# Revit family: Washer_Milnor_35lb-45lb-Capacity_MWT16-18
name_source: partatom
category: Mechanical Equipment
units: mm (PartAtom-declared; Revit-internal decimal feet)

## family parameters
Always vertical = No
Cut with Voids When Loaded = No
Maintain Annotation Orientation = No
OmniClass Number = 23.45.70.11.14.11
OmniClass Title = Washing Machines
Part Type = Normal
Room Calculation Point = No
Round Connector Dimension = Use Diameter
Shared = No
Work Plane-Based = Yes

## types (2) — shared parameters
Assembly Code = E1010610
Construction Details = https://www.arcat.com
Cylinder Depth = 1' - 10"
Cylinder Diameter = 2' - 6"
Default Elevation = 4' - 0"
Description = Milnor Commercial Washer Extractor
Door Base from FF = 1' - 8 1/4"
Door Opening = 1' - 6"
Door Opening Depth = 1' - 5 5/8"
Dynamic Load = 0.00 kip
Expected Lifespan (Years) = 12
Extraction G-Force = 90 Gs
Frequency = 60 Hz
Green Building-LEED = https://www.arcat.com
Installation-Fabrication = https://www.arcat.com
Keynote = 11110
MEP Amperage = 7 A
Manufacturer = Pellerin Milnor Corp
Manufacturer Fax = 504-468-3094
Manufacturer Website = http://www.milnor.com
Number of Poles = 1
Overall Depth = 4' - 4 11/16"
Phase = 3
Product Data = http://www.arcat.com
Product Properties = https://www.arcat.com
Revision = R1_04-2011
Sales Information = http://www.milnor.com
Send Message = http://www.arcat.com
SpecWizard = https://www.arcat.com
Specification = https://www.arcat.com
Suspension Type = Rigid
URL = http://www.milnor.com
Unit Height = 3' - 7 3/16"
Unit Weight = 496
Unit Width = 2' - 5 3/8"
Voltage_MEP = 45 V
Warranty Duration (Years) = 5
doorgas = 1' - 8 1/2"
zero-valued in all types: Cylinder Volume, Maintenance Schedule (Months), Vibration Frequency

## per-type parameters (varying)
| type | Capacity | Unit Depth |
| MWT16X5AE2018125D | 35 lb | 3' - 6 1/8" |
| MWT18X4AE2018125D | 45 lb | 3' - 11 7/16" |

note: column(s) folded — value = type name in every type: Model

## geometry (parser evidence)
native form markers: Sweep x2
no freeform markers — native parametric forms only
